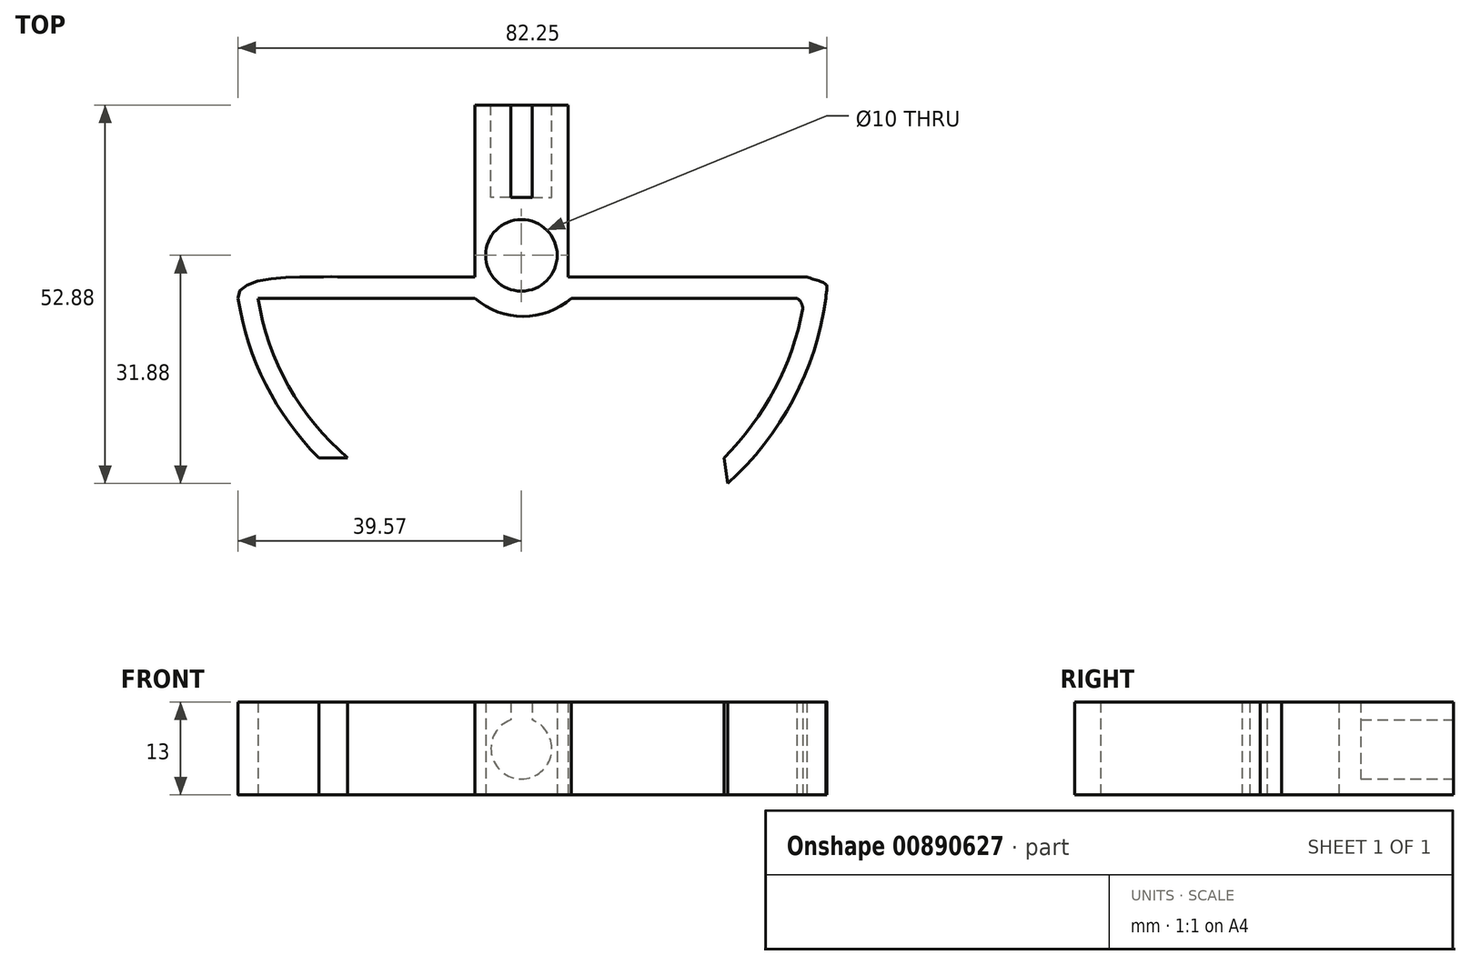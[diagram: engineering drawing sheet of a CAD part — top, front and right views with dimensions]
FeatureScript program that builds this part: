
annotation { "Feature Type Name" : "Feature", "Feature Type Description" : "" }
export const myFeature = defineFeature(function(context is Context, id is Id, definition is map)
    precondition{}
    {
        {
            var Q0;
            Q0=qCreatedBy(makeId("Top.planeOp"),FACE);
            var sketch = newSketch(context, id + "F0", { "sketchPlane" : qUnion([Q0])});
            skCircle(sketch, "E0", {"center": v(0, 0) * mm, "radius": 40 * mm, "construction": true});
            skLineSegment(sketch, "E1", {"start": v(0, 0) * mm, "end": v(-28.28, -28.28) * mm, "construction": true});
            skLineSegment(sketch, "E2", {"start": v(0, 0) * mm, "end": v(28.28, -28.28) * mm, "construction": true});
            skLineSegment(sketch, "E3", {"start": v(-39.89, -3) * mm, "end": v(39.89, -3) * mm, "construction": true});
            skLineSegment(sketch, "E4", {"start": v(-10.02, -3) * mm, "end": v(7, -3) * mm});
            skArc(sketch, "E5", {"start": v(-28.28, -28.28) * mm, "mid": v(-35.7, -18.04) * mm, "end": v(-39.55, -6) * mm});
            skFitSpline(sketch, "E6", {"points": [v(-39.55, -6) * mm, v(-28.95, -3) * mm, v(-24.4, -3) * mm, v(-19.32, -3) * mm, v(-10.02, -3) * mm], "startDerivative": vector(-4.28, 28.2) * mm, "endDerivative": vector(0.87, 0) * mm});
            skLineSegment(sketch, "E7", {"start": v(-39.55, -6) * mm, "end": v(39.55, -6) * mm});
            skLineSegment(sketch, "E8", {"start": v(-28.28, -28.28) * mm, "end": v(28.28, -28.28) * mm, "construction": true});
            skArc(sketch, "E9", {"start": v(-24.28, -28.28) * mm, "mid": v(-32.5, -18.25) * mm, "end": v(-36.8, -6) * mm});
            skArc(sketch, "E10", {"start": v(28.28, -28.28) * mm, "mid": v(35.7, -18.04) * mm, "end": v(39.55, -6) * mm});
            skLineSegment(sketch, "E11", {"start": v(28.28, -28.28) * mm, "end": v(28.8, -31.88) * mm});
            skArc(sketch, "E12", {"start": v(28.8, -31.88) * mm, "mid": v(37.95, -20.15) * mm, "end": v(42.55, -6) * mm});
            skLineSegment(sketch, "E13", {"start": v(-36.8, -6) * mm, "end": v(33.99, -6) * mm});
            skLineSegment(sketch, "E14", {"start": v(-10.02, -3) * mm, "end": v(-10.02, -3) * mm});
            skLineSegment(sketch, "E15", {"start": v(7, -3) * mm, "end": v(39.89, -3) * mm});
            skLineSegment(sketch, "E16", {"start": v(-28.28, -28.28) * mm, "end": v(-24.28, -28.28) * mm});
            skLineSegment(sketch, "E17", {"start": v(39.55, -6) * mm, "end": v(42.55, -6) * mm, "construction": true});
            skFitSpline(sketch, "E18", {"points": [v(39.89, -3) * mm, v(42.55, -4.09) * mm, v(42.55, -6) * mm], "startDerivative": vector(4.21, -2.12) * mm, "endDerivative": vector(0.52, -5.79) * mm});
            skFitSpline(sketch, "E19", {"points": [v(33.99, -6) * mm, v(38.45, -6) * mm, v(39.3, -7.44) * mm], "startDerivative": vector(9.27, -0.07) * mm, "endDerivative": vector(0.7, -5.18) * mm});
            skLineSegment(sketch, "E20", {"start": v(-6.5, 21) * mm, "end": v(-6.5, -3) * mm});
            skLineSegment(sketch, "E21", {"start": v(-6.5, 21) * mm, "end": v(6.5, 21) * mm});
            skLineSegment(sketch, "E22", {"start": v(6.5, 21) * mm, "end": v(6.5, -3) * mm});
            skLineSegment(sketch, "E23", {"start": v(-6.5, -3) * mm, "end": v(-6.5, -6) * mm});
            skLineSegment(sketch, "E24", {"start": v(7, -3) * mm, "end": v(7, -6) * mm});
            skArc(sketch, "E25", {"start": v(-6.5, -6) * mm, "mid": v(0.25, -8.53) * mm, "end": v(7, -6) * mm});
            skSolve(sketch);
        }
        {
            var Q0;
            Q0=qCreatedBy(makeId("Top.planeOp"),FACE);
            var sketch = newSketch(context, id + "F1", { "sketchPlane" : qUnion([Q0])});
            skCircle(sketch, "E26", {"center": v(0, 0) * mm, "radius": 5 * mm});
            skSolve(sketch);
        }
        {
            var Q0;
            Q0 = qSketchRegion(id + "F0", true);
            extrude(context, id + "F2", {"entities" : qUnion([Q0]), "depth" : 13 * mm, "offsetDistance" : 25 * mm});
        }
        {
            var Q0;
            Q0=makeQuery(id+"F1.imprint","IMPRINT",FACE,{"disambiguationData":[TD([[makeQuery(id+"F1.imprint","IMPRINT",EDGE,{"derivedFrom":sQuery(id+"F1.wireOp",EDGE,"E26")}),1.0]])]});
            var Q1;
            Q1=makeQuery(id+"F2.opExtrude","CAP_FACE",FACE,{"disambiguationData":[OSD([sQuery(id+"F0.wireOp",EDGE,"E4"),sQuery(id+"F0.wireOp",EDGE,"E5"),sQuery(id+"F0.wireOp",EDGE,"E6"),sQuery(id+"F0.wireOp",EDGE,"E9"),sQuery(id+"F0.wireOp",EDGE,"E10"),sQuery(id+"F0.wireOp",EDGE,"E11"),sQuery(id+"F0.wireOp",EDGE,"E12"),sQuery(id+"F0.wireOp",EDGE,"E13"),sQuery(id+"F0.wireOp",EDGE,"E14"),sQuery(id+"F0.wireOp",EDGE,"E15"),sQuery(id+"F0.wireOp",EDGE,"E16"),sQuery(id+"F0.wireOp",EDGE,"E18"),sQuery(id+"F0.wireOp",EDGE,"E19"),sQuery(id+"F0.wireOp",EDGE,"E20"),sQuery(id+"F0.wireOp",EDGE,"E21"),sQuery(id+"F0.wireOp",EDGE,"E22"),sQuery(id+"F0.wireOp",EDGE,"E25")])],"isStart":false});
            extrude(context, id + "F3", {"entities" : qUnion([Q0]), "operationType" : NewBodyOperationType.REMOVE, "endBound" : BoundingType.UP_TO_SURFACE, "depth" : 25 * mm, "endBoundEntityFace" : qUnion([Q1]), "offsetDistance" : 25 * mm});
        }
        {
            var Q0;
            Q0=makeQuery(id+"F2.opExtrude","SWEPT_FACE",FACE,{"disambiguationData":[OSD([sQuery(id+"F0.wireOp",EDGE,"E21")])]});
            var sketch = newSketch(context, id + "F4", { "sketchPlane" : qUnion([Q0])});
            skLineSegment(sketch, "E27", {"start": v(-6.5, 6.5) * mm, "end": v(0, 6.5) * mm, "construction": true});
            skCircle(sketch, "E28", {"center": v(0, 6.5) * mm, "radius": 4.25 * mm});
            skLineSegment(sketch, "E29", {"start": v(-1.5, 13) * mm, "end": v(-1.5, 10.48) * mm});
            skLineSegment(sketch, "E30", {"start": v(1.5, 13) * mm, "end": v(1.5, 10.48) * mm});
            skSolve(sketch);
        }
        {
            var Q0;
            {var subQ0=sQuery(id+"F4.wireOp",EDGE,"E28");var subQ1=makeQuery(id+"F4.imprint","INTERSECT",VERTEX,{"derivedFrom":[subQ0,sQuery(id+"F4.wireOp",EDGE,"E29")]});Q0=makeQuery(id+"F4.imprint","IMPRINT",FACE,{"disambiguationData":[TD([[makeQuery(id+"F4.imprint","IMPRINT",EDGE,{"disambiguationData":[TD([[subQ1,1.0]])],"derivedFrom":subQ0}),1.0]])]});}
            var Q1;
            {var subQ0=sQuery(id+"F4.wireOp",EDGE,"E29");Q1=makeQuery(id+"F4.imprint","IMPRINT",FACE,{"disambiguationData":[TD([[makeQuery(id+"F4.imprint","IMPRINT",EDGE,{"derivedFrom":subQ0}),1.0]])]});}
            extrude(context, id + "F5", {"entities" : qUnion([Q0, Q1]), "operationType" : NewBodyOperationType.REMOVE, "oppositeDirection" : true, "depth" : 12.9 * mm, "offsetDistance" : 25 * mm});
        }
    });
